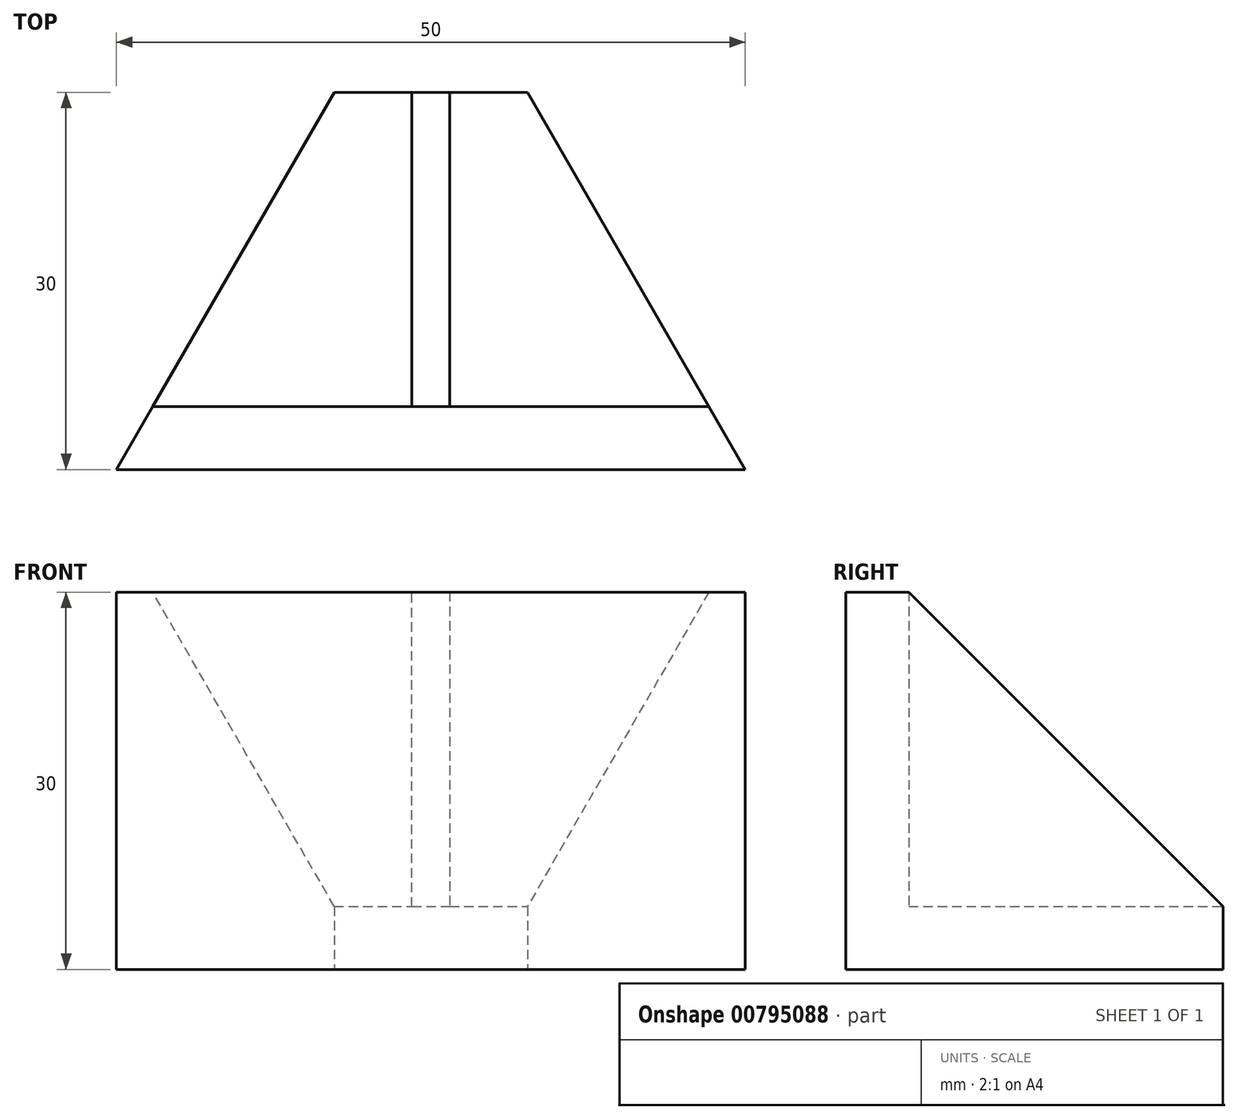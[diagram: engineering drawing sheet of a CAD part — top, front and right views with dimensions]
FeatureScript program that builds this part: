
annotation { "Feature Type Name" : "Feature", "Feature Type Description" : "" }
export const myFeature = defineFeature(function(context is Context, id is Id, definition is map)
    precondition{}
    {
        {
            var Q0;
            Q0=qCreatedBy(makeId("Top.planeOp"),FACE);
            var sketch = newSketch(context, id + "F0", { "sketchPlane" : qUnion([Q0])});
            skPoint(sketch, "E0.middle", {"position": v(0, 0) * mm});
            skLineSegment(sketch, "E1", {"start": v(-7.68, 21.3) * mm, "end": v(7.68, 21.3) * mm});
            skLineSegment(sketch, "E2", {"start": v(7.68, 21.3) * mm, "end": v(25, -8.7) * mm});
            skLineSegment(sketch, "E3", {"start": v(25, -8.7) * mm, "end": v(-25, -8.7) * mm});
            skLineSegment(sketch, "E4", {"start": v(-25, -8.7) * mm, "end": v(-7.68, 21.3) * mm});
            skSolve(sketch);
        }
        {
            var Q0;
            Q0=makeQuery(id+"F0.imprint","IMPRINT",FACE,{"disambiguationData":[TD([[makeQuery(id+"F0.imprint","IMPRINT",EDGE,{"derivedFrom":sQuery(id+"F0.wireOp",EDGE,"E1")}),-1.0]])]});
            extrude(context, id + "F1", {"entities" : qUnion([Q0]), "depth" : 5 * mm, "offsetDistance" : 25 * mm});
        }
        {
            var Q0;
            Q0=makeQuery(id+"F1.opExtrude","CAP_FACE",FACE,{"disambiguationData":[OSD([sQuery(id+"F0.wireOp",EDGE,"E1"),sQuery(id+"F0.wireOp",EDGE,"E2"),sQuery(id+"F0.wireOp",EDGE,"E3"),sQuery(id+"F0.wireOp",EDGE,"E4")])],"isStart":false});
            var sketch = newSketch(context, id + "F2", { "sketchPlane" : qUnion([Q0])});
            skLineSegment(sketch, "E5", {"start": v(-1.5, 21.3) * mm, "end": v(-1.5, -3.7) * mm});
            skLineSegment(sketch, "E6", {"start": v(-1.5, -3.7) * mm, "end": v(1.5, -3.7) * mm});
            skLineSegment(sketch, "E7", {"start": v(1.5, -3.7) * mm, "end": v(1.5, 21.3) * mm});
            skSolve(sketch);
        }
        {
            var Q0;
            Q0=qCreatedBy(makeId("Right.planeOp"),FACE);
            var sketch = newSketch(context, id + "F3", { "sketchPlane" : qUnion([Q0])});
            skPoint(sketch, "E8.0", {"position": v(21.3, 5) * mm});
            skLineSegment(sketch, "E9", {"start": v(21.3, 5) * mm, "end": v(-3.7, 30) * mm});
            skLineSegment(sketch, "E10", {"start": v(-3.7, 30) * mm, "end": v(21.3, 30) * mm});
            skLineSegment(sketch, "E11", {"start": v(21.3, 30) * mm, "end": v(21.3, 5) * mm});
            skSolve(sketch);
        }
        {
            var Q0;
            {var subQ2=sQuery(id+"F2.wireOp",EDGE,"E5");Q0=makeQuery(id+"F2.imprint","IMPRINT",FACE,{"disambiguationData":[TD([[makeQuery(id+"F2.imprint","IMPRINT",EDGE,{"derivedFrom":subQ2}),-1.0]])]});}
            var Q1;
            Q1=sQuery(id+"F3.wireOp",VERTEX,"E9.end");
            extrude(context, id + "F4", {"entities" : qUnion([Q0]), "operationType" : NewBodyOperationType.ADD, "endBound" : BoundingType.UP_TO_VERTEX, "depth" : 25 * mm, "endBoundEntityVertex" : qUnion([Q1]), "offsetDistance" : 25 * mm});
        }
        {
            var Q0;
            Q0=makeQuery(id+"F3.imprint","IMPRINT",FACE,{"disambiguationData":[TD([[makeQuery(id+"F3.imprint","IMPRINT",EDGE,{"derivedFrom":sQuery(id+"F3.wireOp",EDGE,"E9")}),-1.0]])]});
            var Q1;
            {var subQ0=sQuery(id+"F0.wireOp",EDGE,"E4");Q1=makeQuery(id+"F4.boolean.opBoolean","MERGE",FACE,{"derivedFrom":[makeQuery(id+"F1.opExtrude","SWEPT_FACE",FACE,{"disambiguationData":[OSD([subQ0])]}),makeQuery(id+"F4.opExtrude","SWEPT_FACE",FACE,{"disambiguationData":[OSD([subQ0])]})]});}
            var Q2;
            {var subQ0=sQuery(id+"F0.wireOp",EDGE,"E2");Q2=makeQuery(id+"F4.boolean.opBoolean","MERGE",FACE,{"derivedFrom":[makeQuery(id+"F1.opExtrude","SWEPT_FACE",FACE,{"disambiguationData":[OSD([subQ0])]}),makeQuery(id+"F4.opExtrude","SWEPT_FACE",FACE,{"disambiguationData":[OSD([subQ0])]})]});}
            extrude(context, id + "F5", {"entities" : qUnion([Q0]), "operationType" : NewBodyOperationType.REMOVE, "endBound" : BoundingType.UP_TO_SURFACE, "oppositeDirection" : true, "depth" : 25 * mm, "endBoundEntityFace" : qUnion([Q1]), "offsetDistance" : 25 * mm, "hasSecondDirection" : true, "secondDirectionBound" : SecondDirectionBoundingType.UP_TO_SURFACE, "secondDirectionOppositeDirection" : false, "secondDirectionDepth" : 25 * mm, "secondDirectionBoundEntityFace" : qUnion([Q2])});
        }
    });
